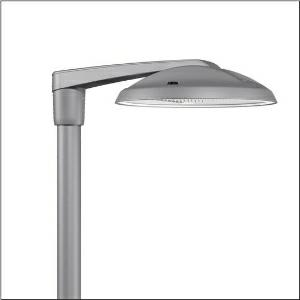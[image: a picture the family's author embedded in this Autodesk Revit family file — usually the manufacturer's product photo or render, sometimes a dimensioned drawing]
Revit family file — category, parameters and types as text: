
# Revit family: dl_50_iq_mini___st1_0a_5xa248d31v08ne_add0
name_source: partatom
category: Lighting Fixtures
units: mm (PartAtom-declared; Revit-internal decimal feet)

## family parameters
Cut with Voids When Loaded = No
Host = Face
Light Source = No
Part Type = Normal
Room Calculation Point = No
Round Connector Dimension = Use Diameter
Shared = No

## types (1)
- --- (1 x LED, 17900 lm, 110.1 W, 3000K)
    Apparent Load = 110 VA
    CIE Flux Codes = 37 72 97 100 100
    Color Rendering = 70
    Color Temperature = 3000K
    Default Elevation = 1800 mm
    Description = DL 50 iQ mini, mast luminaire, primary light control with lens, of PMMA, primary optical cover: cover, of toughened safety glass, transparent, light distribution: ST1.0a, light emission: direct distribution, primary light characteristic: asymmetric, installation type: post-top, side-entry, LED, High Power LED, rated luminous flux: 17.900lm, luminous efficacy: 163lm/W, light colour: 730, colour temperature: 3000K, control gear: iQ-Street Remote, D4i with power reduction, control: optimised constant luminous flux control (CLO 2.0), Desk-Remote (wireless, voltage-free reading and setting of iQ features in the workshop via application-optimized NFC function/RFID function), Light-Fading, Smart-Wire, Night-Set, Lumen-Switch, Temp-Guard, Auto-Match, Street-Remote, pre-setting: logarithmic dimming characteristic, mains connection: 230..240V, AC, 50/60Hz, connection cable pre-assembled, cable length: 10,5m, start of lifetime: 110W, end of service life: 116W, reduction: 50W, luminaire housing, of diecast aluminium, powder-coated, SITECO metallic grey (DB 702S), inclination adjustable: 0°, 5°, 10° (post-top) | 0°, -5°, -10°, -15° (side-entry), please order mast post-top element or mast side-entry element separately, diameter: 500mm, height: 115mm, post-top: for spigot size d x l = 76 x 100mm; with reducer (optional accessory) 60 x 100mm | side-entry: for spigot size d x l = 60 x 100mm; with reducer (optional accessory) 42 x 100mm, mounting height: 4..6m, Smart Interface above, protection rating (complete): IP66, insulation class (complete): insulation class II (safety insulation), certification: CE, ENEC, ENEC+, VDE, impact resistance: IK08, permissible operating ambient temperature for outdoor applications: -25..+40°C, standard-compliant lighting for roads and squares, packaging unit: 1 piece

Light Distribution: ST1.0a
    Height = 115 mm
    Lamp = 1 x LED
    Lamp Light Flux = 17900 lm
    Lamp Power = 110.1 W
    Lamp count = 1
    Length = 500 mm
    Luminous efficacy = 163 lm/W
    Manufacturer = Siteco
    ModVariant = No
    Model = 5XA248D31V08NE
    Number of Poles = 1
    OnlyDefault = Yes
    Power Factor = 1
    Product Name = DL 50 iQ mini | ST1.0a
    Product group = mast luminaire | pylon top
    ProductGroupID = 6100
    Protection Class = Protection class II
    Protection Degree = IP 66
    RLX_Detail_Level = 1
    RLX_Emergency_Light_Flux = 0 lm
    RLX_Emergency_Type = 0
    RLX_Emergency_Type_DB = No
    RlxData = <blob elided: 106429 chars, md5=e73d5bd2>
    Socket = socket
    Standby Power = 0 W
    System Light Flux = 17900 lm
    System Power = 110 W
    Type Comments = factory setting: luminous flux: 100 % | dim-lin: 254 | 601 mA
    Type Image = l_1251788.jpg
    URL = http://relux.com
    VarID = @adj_072977
    Voltage = 0 V
    Weight = 0.00 kg
    Width = 0 mm  [stored 0 ft]

note: [stored X ft] marks values corroborated as IEEE doubles in the binary element streams (Revit-internal decimal feet)

## geometry (parser evidence)
native form markers: Blend x4, Sweep x8
no freeform markers — native parametric forms only
